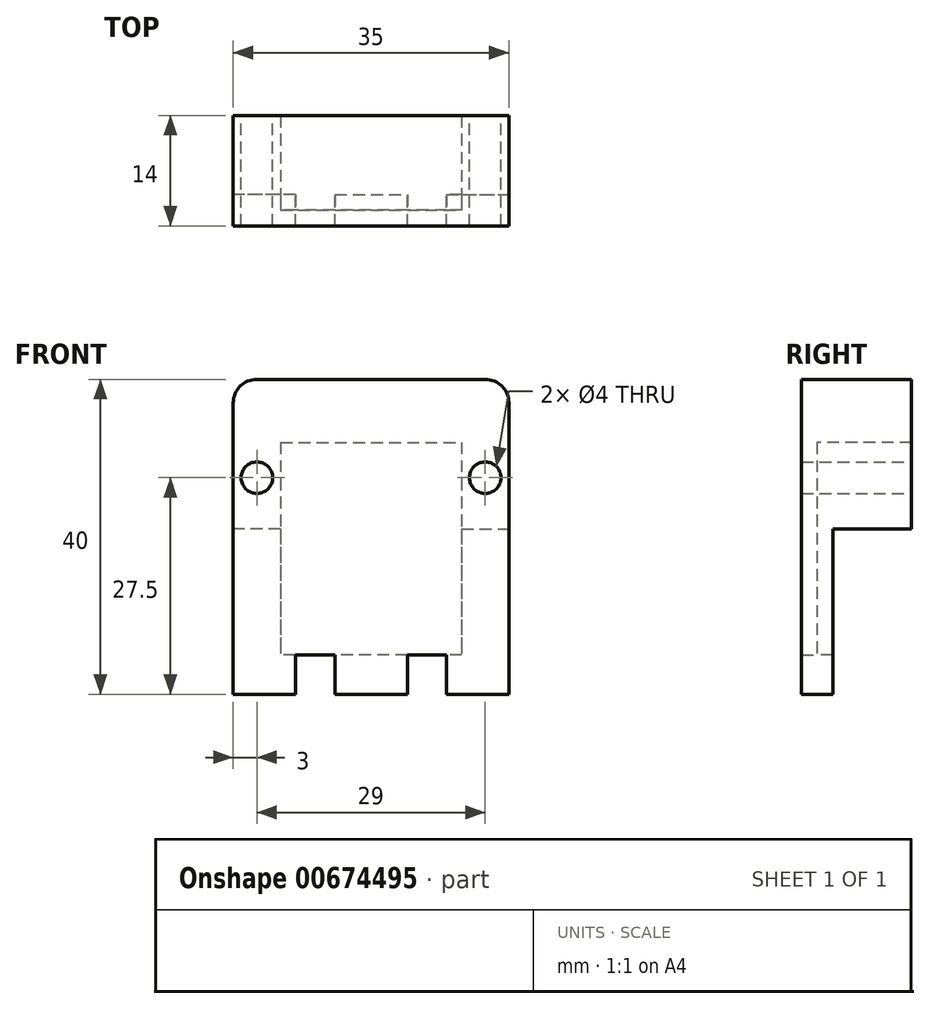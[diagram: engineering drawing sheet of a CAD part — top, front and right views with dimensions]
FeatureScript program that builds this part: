
annotation { "Feature Type Name" : "Feature", "Feature Type Description" : "" }
export const myFeature = defineFeature(function(context is Context, id is Id, definition is map)
    precondition{}
    {
        {
            var Q0;
            Q0=qCreatedBy(makeId("Top.planeOp"),FACE);
            var sketch = newSketch(context, id + "F0", { "sketchPlane" : qUnion([Q0])});
            skFitSpline(sketch, "E0", {"points": [v(-20127.86, 27658) * mm, v(-12586.08, 24319.4) * mm, v(-3861.17, 21221.83) * mm, v(4194.73, 14501.6) * mm]});
            skFitSpline(sketch, "E1", {"points": [v(4132.77, 14556.74) * mm, v(7203.01, 11644.07) * mm, v(10235.91, 8816.2) * mm, v(13962.45, 4413.42) * mm]});
            skFitSpline(sketch, "E2", {"points": [v(13927.46, 4456.6) * mm, v(16683, 903.5) * mm, v(18153.38, -2176.17) * mm, v(18736.35, -4928.93) * mm]});
            skFitSpline(sketch, "E3", {"points": [v(18764.68, -5038.8) * mm, v(19701.3, -8110.08) * mm, v(20785.76, -12106.02) * mm, v(19759.32, -15005.87) * mm]});
            skFitSpline(sketch, "E4", {"points": [v(19822.8, -14856.79) * mm, v(17400.69, -19685.58) * mm, v(16344.3, -19633.9) * mm, v(14984.19, -20667.53) * mm]});
            skFitSpline(sketch, "E5", {"points": [v(14991.67, -20661.88) * mm, v(9421.66, -24831.87) * mm, v(6898.53, -24451.46) * mm, v(3764.11, -25600.76) * mm]});
            skFitSpline(sketch, "E6", {"points": [v(3976.36, -25542.77) * mm, v(-3565.49, -26930.7) * mm, v(-10775.44, -27745.3) * mm, v(-18500.93, -28140.45) * mm]});
            skFitSpline(sketch, "E7.0", {"points": [v(4211.65, -26821.3) * mm, v(3261.92, -26996.08) * mm, v(1372.6, -27327.64) * mm, v(-1440.62, -27772.75) * mm, v(-4242.8, -28167.35) * mm, v(-7043.6, -28513.23) * mm, v(-9852.69, -28812.16) * mm, v(-12679.76, -29065.94) * mm, v(-15534.5, -29276.4) * mm, v(-17462.61, -29389.04) * mm, v(-18434.53, -29438.75) * mm]});
            skFitSpline(sketch, "E7.1", {"points": [v(15770.77, -21702.56) * mm, v(15411.33, -21971.66) * mm, v(14889, -22348.97) * mm, v(14223.5, -22803.63) * mm, v(13739.16, -23121.46) * mm, v(13268.96, -23417.18) * mm, v(12812.26, -23691.8) * mm, v(12368.46, -23946.35) * mm, v(11936.98, -24181.84) * mm, v(11517.28, -24399.26) * mm, v(11108.86, -24599.61) * mm, v(10711.26, -24783.9) * mm, v(10324.05, -24953.1) * mm, v(9946.86, -25108.26) * mm, v(9579.34, -25250.38) * mm, v(9221.2, -25380.5) * mm, v(8872.14, -25499.69) * mm, v(8531.9, -25609.01) * mm, v(8200.2, -25709.58) * mm, v(7876.79, -25802.5) * mm, v(7561.34, -25888.9) * mm, v(7253.54, -25969.92) * mm, v(6953, -26046.69) * mm, v(6659.27, -26120.32) * mm, v(6371.85, -26191.94) * mm, v(6090.15, -26262.62) * mm, v(5813.51, -26333.44) * mm, v(5541.18, -26405.47) * mm, v(5272.31, -26479.73) * mm, v(5005.98, -26557.26) * mm, v(4741.2, -26639.12) * mm, v(4476.9, -26726.35) * mm, v(4300.26, -26788.8) * mm, v(4211.65, -26821.3) * mm]});
            skFitSpline(sketch, "E7.2", {"points": [v(20984.81, -15439.65) * mm, v(20829.08, -15750.12) * mm, v(20527.43, -16334.17) * mm, v(20101.27, -17108.83) * mm, v(19765.34, -17677.57) * mm, v(19506.43, -18091.02) * mm, v(19316.71, -18381.43) * mm, v(19131.05, -18653.27) * mm, v(18949, -18907.57) * mm, v(18770.17, -19145.34) * mm, v(18594.18, -19367.53) * mm, v(18420.71, -19575.03) * mm, v(18249.5, -19768.65) * mm, v(18080.4, -19949.15) * mm, v(17913.34, -20117.2) * mm, v(17748.42, -20273.46) * mm, v(17585.87, -20418.51) * mm, v(17426.07, -20552.95) * mm, v(17269.5, -20677.38) * mm, v(17116.73, -20792.48) * mm, v(16968.38, -20898.98) * mm, v(16825.01, -20997.69) * mm, v(16687.11, -21089.5) * mm, v(16555, -21175.4) * mm, v(16428.76, -21256.37) * mm, v(16308.3, -21333.51) * mm, v(16193.2, -21407.92) * mm, v(16082.83, -21480.73) * mm, v(15976.33, -21553.15) * mm, v(15872.68, -21626.44) * mm, v(15804.69, -21676.78) * mm, v(15770.77, -21702.56) * mm]});
            skFitSpline(sketch, "E7.3", {"points": [v(-19601.64, 28846.74) * mm, v(-19134.48, 28639.93) * mm, v(-18189.2, 28227.4) * mm, v(-16741.29, 27606.4) * mm, v(-15266.3, 26977.67) * mm, v(-13767.13, 26335.65) * mm, v(-12246.7, 25674.72) * mm, v(-10707.95, 24989.2) * mm, v(-9153.8, 24273.35) * mm, v(-7587.2, 23521.43) * mm, v(-6011.12, 22727.67) * mm, v(-4428.59, 21886.27) * mm, v(-2842.61, 20991.44) * mm, v(-1256.28, 20037.4) * mm, v(327.31, 19018.38) * mm, v(1905.02, 17928.67) * mm, v(3473.66, 16762.57) * mm, v(4511.26, 15930.5) * mm, v(5027.48, 15499.86) * mm]});
            skFitSpline(sketch, "E7.4", {"points": [v(5027.48, 15499.86) * mm, v(5219.04, 15318.14) * mm, v(5602.27, 14954.96) * mm, v(6178.54, 14408.6) * mm, v(6757.27, 13858.2) * mm, v(7339.51, 13301.38) * mm, v(7926.25, 12735.75) * mm, v(8715.88, 11966.65) * mm, v(9719.03, 10971.4) * mm, v(10956.2, 9704.14) * mm, v(12234.3, 8345.24) * mm, v(13560.97, 6876.07) * mm, v(14483, 5810.64) * mm, v(14954.73, 5253.3) * mm]});
            skFitSpline(sketch, "E7.5", {"points": [v(14954.73, 5253.3) * mm, v(15309.89, 4795.34) * mm, v(15980.45, 3892.56) * mm, v(16871.36, 2575.43) * mm, v(17521.47, 1506.84) * mm, v(17988.15, 668.28) * mm, v(18311.92, 47.28) * mm, v(18609.94, -566.05) * mm, v(18882.64, -1171.94) * mm, v(19130.48, -1770.6) * mm, v(19353.89, -2362.18) * mm, v(19553.3, -2946.88) * mm, v(19729.14, -3524.8) * mm, v(19881.84, -4096.04) * mm, v(19968.51, -4472.48) * mm, v(20008.14, -4659.6) * mm]});
            skFitSpline(sketch, "E7.6", {"points": [v(20008.14, -4659.6) * mm, v(20067.31, -4853.62) * mm, v(20187.24, -5250.33) * mm, v(20368.4, -5868.17) * mm, v(20547.38, -6505.79) * mm, v(20720.73, -7160.3) * mm, v(20885, -7828.99) * mm, v(21036.66, -8509.21) * mm, v(21172.17, -9198.48) * mm, v(21287.9, -9894.43) * mm, v(21364.72, -10478.06) * mm, v(21412.43, -10946.12) * mm, v(21440.83, -11297.48) * mm, v(21461.31, -11648.9) * mm, v(21473.32, -12000.15) * mm, v(21476.3, -12350.95) * mm, v(21469.62, -12701.07) * mm, v(21452.68, -13050.24) * mm, v(21424.81, -13398.19) * mm, v(21385.33, -13744.6) * mm, v(21333.5, -14089.17) * mm, v(21268.6, -14431.5) * mm, v(21189.82, -14771.16) * mm, v(21096.4, -15107.66) * mm, v(21023.8, -15329.48) * mm, v(20984.81, -15439.65) * mm]});
            skLineSegment(sketch, "E8", {"start": v(18736.35, -4928.93) * mm, "end": v(18764.68, -5038.8) * mm});
            skLineSegment(sketch, "E9", {"start": v(-19601.64, 28846.74) * mm, "end": v(-20127.86, 27658) * mm});
            skLineSegment(sketch, "E10", {"start": v(-18500.93, -28140.45) * mm, "end": v(-18434.53, -29438.75) * mm});
            skSolve(sketch);
        }
        {
            var Q0;
            Q0=qCreatedBy(makeId("Front.planeOp"),FACE);
            var sketch = newSketch(context, id + "F1", { "sketchPlane" : qUnion([Q0])});
            skLineSegment(sketch, "E11.bottom", {"start": v(17.5, -17.5) * mm, "end": v(-17.5, -17.5) * mm});
            skLineSegment(sketch, "E11.top", {"start": v(14.5, 17.5) * mm, "end": v(-14.5, 17.5) * mm});
            skLineSegment(sketch, "E11.left", {"start": v(17.5, -17.5) * mm, "end": v(17.5, 14.5) * mm});
            skLineSegment(sketch, "E11.right", {"start": v(-17.5, -17.5) * mm, "end": v(-17.5, 14.5) * mm});
            skPoint(sketch, "E11.middle", {"position": v(0, 0) * mm});
            skLineSegment(sketch, "E12", {"start": v(-11.5, 9.5) * mm, "end": v(-11.5, -12.5) * mm});
            skLineSegment(sketch, "E13.MirrorCS", {"start": v(11.5, 9.5) * mm, "end": v(11.5, -12.5) * mm});
            skLineSegment(sketch, "E14", {"start": v(-11.5, 9.5) * mm, "end": v(11.5, 9.5) * mm});
            skLineSegment(sketch, "E15", {"start": v(-11.5, -12.5) * mm, "end": v(-11.5, -17.5) * mm});
            skLineSegment(sketch, "E16.MirrorCS", {"start": v(11.5, -12.5) * mm, "end": v(11.5, -17.5) * mm});
            skLineSegment(sketch, "E17", {"start": v(-4.6, -17.5) * mm, "end": v(-4.6, -22.5) * mm});
            skLineSegment(sketch, "E18", {"start": v(-4.6, -22.5) * mm, "end": v(0, -22.5) * mm});
            skLineSegment(sketch, "E19", {"start": v(-9.6, -17.5) * mm, "end": v(-9.6, -22.5) * mm});
            skLineSegment(sketch, "E20", {"start": v(-9.6, -22.5) * mm, "end": v(-17.5, -22.5) * mm});
            skLineSegment(sketch, "E21", {"start": v(0, -22.5) * mm, "end": v(0, -17.5) * mm});
            skLineSegment(sketch, "E22", {"start": v(-17.5, -22.5) * mm, "end": v(-17.5, -17.5) * mm});
            skLineSegment(sketch, "E23.MirrorCS", {"start": v(4.6, -22.5) * mm, "end": v(0, -22.5) * mm});
            skLineSegment(sketch, "E24.MirrorCS", {"start": v(4.6, -17.5) * mm, "end": v(4.6, -22.5) * mm});
            skLineSegment(sketch, "E25.MirrorCS", {"start": v(9.6, -17.5) * mm, "end": v(9.6, -22.5) * mm});
            skLineSegment(sketch, "E26.MirrorCS", {"start": v(9.6, -22.5) * mm, "end": v(17.5, -22.5) * mm});
            skLineSegment(sketch, "E27.MirrorCS", {"start": v(17.5, -22.5) * mm, "end": v(17.5, -17.5) * mm});
            skCircle(sketch, "E28", {"center": v(-14.5, 5) * mm, "radius": 2 * mm});
            skCircle(sketch, "E29.MirrorC", {"center": v(14.5, 5) * mm, "radius": 2 * mm});
            skLineSegment(sketch, "E30", {"start": v(-11.5, 5) * mm, "end": v(-14.5, 5) * mm, "construction": true});
            skLineSegment(sketch, "E31", {"start": v(-17.5, 5) * mm, "end": v(-14.5, 5) * mm, "construction": true});
            skPoint(sketch, "E32.visualSharp", {"position": v(17.5, 17.5) * mm});
            skArc(sketch, "E32.filletArc", {"start": v(17.5, 14.5) * mm, "mid": v(16.62, 16.62) * mm, "end": v(14.5, 17.5) * mm});
            skPoint(sketch, "E33.visualSharp", {"position": v(-17.5, 17.5) * mm});
            skArc(sketch, "E33.filletArc", {"start": v(-14.5, 17.5) * mm, "mid": v(-16.62, 16.62) * mm, "end": v(-17.5, 14.5) * mm});
            skLineSegment(sketch, "E34", {"start": v(11.5, -12.5) * mm, "end": v(-11.5, -12.5) * mm});
            skSolve(sketch);
        }
        {
            var Q0;
            Q0=makeQuery(id+"F1.imprint","IMPRINT",FACE,{"disambiguationData":[TD([[makeQuery(id+"F1.imprint","IMPRINT",EDGE,{"derivedFrom":sQuery(id+"F1.wireOp",EDGE,"E11.top")}),1.0]])]});
            var Q1;
            {var subQ0=sQuery(id+"F1.wireOp",EDGE,"E12");Q1=makeQuery(id+"F1.imprint","IMPRINT",FACE,{"disambiguationData":[TD([[makeQuery(id+"F1.imprint","IMPRINT",EDGE,{"derivedFrom":subQ0}),1.0]])]});}
            var Q2;
            {var subQ3=sQuery(id+"F1.wireOp",EDGE,"E15");Q2=makeQuery(id+"F1.imprint","IMPRINT",FACE,{"disambiguationData":[TD([[makeQuery(id+"F1.imprint","IMPRINT",EDGE,{"derivedFrom":subQ3}),1.0]])]});}
            var Q3;
            {var subQ0=sQuery(id+"F1.wireOp",EDGE,"E17");Q3=makeQuery(id+"F1.imprint","IMPRINT",FACE,{"disambiguationData":[TD([[makeQuery(id+"F1.imprint","IMPRINT",EDGE,{"derivedFrom":subQ0}),1.0]])]});}
            var Q4;
            {var subQ0=sQuery(id+"F1.wireOp",EDGE,"E21");Q4=makeQuery(id+"F1.imprint","IMPRINT",FACE,{"disambiguationData":[TD([[makeQuery(id+"F1.imprint","IMPRINT",EDGE,{"derivedFrom":subQ0}),-1.0]])]});}
            var Q5;
            {var subQ0=sQuery(id+"F1.wireOp",EDGE,"E25.MirrorCS");Q5=makeQuery(id+"F1.imprint","IMPRINT",FACE,{"disambiguationData":[TD([[makeQuery(id+"F1.imprint","IMPRINT",EDGE,{"derivedFrom":subQ0}),1.0]])]});}
            var Q6;
            {var subQ3=sQuery(id+"F1.wireOp",EDGE,"E19");Q6=makeQuery(id+"F1.imprint","IMPRINT",FACE,{"disambiguationData":[TD([[makeQuery(id+"F1.imprint","IMPRINT",EDGE,{"derivedFrom":subQ3}),-1.0]])]});}
            extrude(context, id + "F2", {"entities" : qUnion([Q0, Q1, Q2, Q3, Q4, Q5, Q6]), "depth" : 2 * mm, "offsetDistance" : 25 * mm});
        }
        {
            var Q0;
            Q0=makeQuery(id+"F1.imprint","IMPRINT",FACE,{"disambiguationData":[TD([[makeQuery(id+"F1.imprint","IMPRINT",EDGE,{"derivedFrom":sQuery(id+"F1.wireOp",EDGE,"E11.top")}),1.0]])]});
            var Q1;
            {var subQ0=sQuery(id+"F1.wireOp",EDGE,"E25.MirrorCS");Q1=makeQuery(id+"F1.imprint","IMPRINT",FACE,{"disambiguationData":[TD([[makeQuery(id+"F1.imprint","IMPRINT",EDGE,{"derivedFrom":subQ0}),1.0]])]});}
            var Q2;
            {var subQ3=sQuery(id+"F1.wireOp",EDGE,"E19");Q2=makeQuery(id+"F1.imprint","IMPRINT",FACE,{"disambiguationData":[TD([[makeQuery(id+"F1.imprint","IMPRINT",EDGE,{"derivedFrom":subQ3}),-1.0]])]});}
            var Q3;
            {var subQ0=sQuery(id+"F1.wireOp",EDGE,"E17");Q3=makeQuery(id+"F1.imprint","IMPRINT",FACE,{"disambiguationData":[TD([[makeQuery(id+"F1.imprint","IMPRINT",EDGE,{"derivedFrom":subQ0}),1.0]])]});}
            var Q4;
            {var subQ0=sQuery(id+"F1.wireOp",EDGE,"E21");Q4=makeQuery(id+"F1.imprint","IMPRINT",FACE,{"disambiguationData":[TD([[makeQuery(id+"F1.imprint","IMPRINT",EDGE,{"derivedFrom":subQ0}),-1.0]])]});}
            extrude(context, id + "F3", {"entities" : qUnion([Q0, Q1, Q2, Q3, Q4]), "operationType" : NewBodyOperationType.ADD, "oppositeDirection" : true, "depth" : 2 * mm, "offsetDistance" : 25 * mm});
        }
        {
            var Q0;
            Q0=makeQuery(id+"F3.opExtrude","CAP_FACE",FACE,{"disambiguationData":[OSD([sQuery(id+"F1.wireOp",EDGE,"E11.bottom"),sQuery(id+"F1.wireOp",EDGE,"E11.top"),sQuery(id+"F1.wireOp",EDGE,"E11.left"),sQuery(id+"F1.wireOp",EDGE,"E11.right"),sQuery(id+"F1.wireOp",EDGE,"E12"),sQuery(id+"F1.wireOp",EDGE,"E13.MirrorCS"),sQuery(id+"F1.wireOp",EDGE,"E14"),sQuery(id+"F1.wireOp",EDGE,"E15"),sQuery(id+"F1.wireOp",EDGE,"E16.MirrorCS"),sQuery(id+"F1.wireOp",EDGE,"A2bO8YKx-rgoD-gtLu-Rlze-mw0JCP4wLSSP"),sQuery(id+"F1.wireOp",EDGE,"E28"),sQuery(id+"F1.wireOp",EDGE,"E29.MirrorC")])],"isStart":false});
            var sketch = newSketch(context, id + "F4", { "sketchPlane" : qUnion([Q0])});
            skLineSegment(sketch, "E35", {"start": v(-11.5, -1.5) * mm, "end": v(-17.5, -1.5) * mm});
            skLineSegment(sketch, "E36.MirrorCS", {"start": v(11.5, -1.5) * mm, "end": v(17.5, -1.5) * mm});
            skSolve(sketch);
        }
        {
            var Q0;
            {var subQ2=sQuery(id+"F4.wireOp",EDGE,"E35");Q0=makeQuery(id+"F4.imprint","IMPRINT",FACE,{"disambiguationData":[TD([[makeQuery(id+"F4.imprint","IMPRINT",EDGE,{"derivedFrom":subQ2}),-1.0]])]});}
            extrude(context, id + "F5", {"entities" : qUnion([Q0]), "operationType" : NewBodyOperationType.ADD, "depth" : 10 * mm, "offsetDistance" : 25 * mm});
        }
    });
